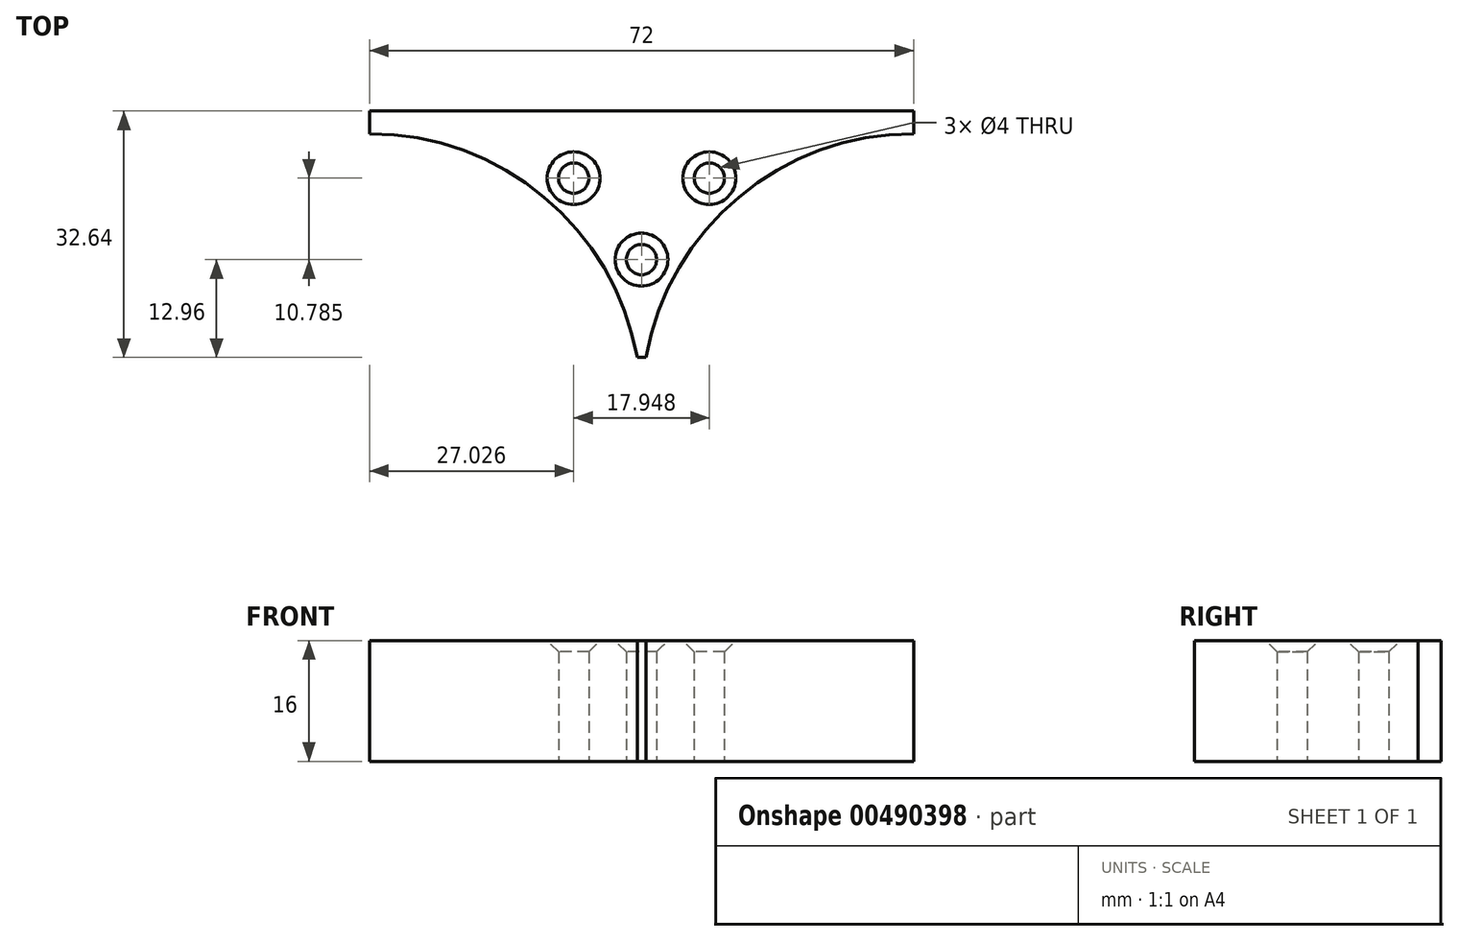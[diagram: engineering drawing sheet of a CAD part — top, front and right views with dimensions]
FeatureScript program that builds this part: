
annotation { "Feature Type Name" : "Feature", "Feature Type Description" : "" }
export const myFeature = defineFeature(function(context is Context, id is Id, definition is map)
    precondition{}
    {
        {
            var Q0;
            Q0=qCreatedBy(makeId("Top.planeOp"),FACE);
            var sketch = newSketch(context, id + "F0", { "sketchPlane" : qUnion([Q0])});
            skArc(sketch, "E0", {"start": v(-0.57, 6.36) * mm, "mid": v(-12.9, 27.61) * mm, "end": v(-36, 36) * mm});
            skArc(sketch, "E1.MirrorC", {"start": v(0.57, 6.36) * mm, "mid": v(12.9, 27.61) * mm, "end": v(36, 36) * mm});
            skLineSegment(sketch, "E2", {"start": v(-0.57, 6.36) * mm, "end": v(0.57, 6.36) * mm});
            skLineSegment(sketch, "E3", {"start": v(-36, 36) * mm, "end": v(-36, 39) * mm});
            skLineSegment(sketch, "E4", {"start": v(-36, 39) * mm, "end": v(0, 39) * mm});
            skLineSegment(sketch, "E5.MirrorCS", {"start": v(-36, 42) * mm, "end": v(-36, 39) * mm});
            skLineSegment(sketch, "E6.MirrorCS", {"start": v(36, 39) * mm, "end": v(0, 39) * mm});
            skLineSegment(sketch, "E7.MirrorCS", {"start": v(36, 36) * mm, "end": v(36, 39) * mm});
            skCircle(sketch, "E8", {"center": v(-36, 0) * mm, "radius": 35.5 * mm, "construction": true});
            skCircle(sketch, "E9", {"center": v(36, 0) * mm, "radius": 35.5 * mm, "construction": true});
            skCircle(sketch, "E10", {"center": v(0, 19.32) * mm, "radius": 2 * mm});
            skCircle(sketch, "E11", {"center": v(-8.97, 30.1) * mm, "radius": 2 * mm});
            skCircle(sketch, "E12.MirrorC", {"center": v(8.97, 30.1) * mm, "radius": 2 * mm});
            skSolve(sketch);
        }
        {
            var Q0;
            Q0=makeQuery(id+"F0.imprint","IMPRINT",FACE,{"disambiguationData":[TD([[makeQuery(id+"F0.imprint","IMPRINT",EDGE,{"derivedFrom":sQuery(id+"F0.wireOp",EDGE,"E0")}),-1.0]])]});
            extrude(context, id + "F1", {"entities" : qUnion([Q0]), "depth" : 16 * mm, "offsetDistance" : 25 * mm});
        }
        {
            var Q0;
            Q0=makeQuery(id+"F1.opExtrude","CAP_EDGE",EDGE,{"disambiguationData":[OSD([sQuery(id+"F0.wireOp",EDGE,"E11")])],"isStart":false});
            var Q1;
            Q1=makeQuery(id+"F1.opExtrude","CAP_EDGE",EDGE,{"disambiguationData":[OSD([sQuery(id+"F0.wireOp",EDGE,"E10")])],"isStart":false});
            var Q2;
            Q2=makeQuery(id+"F1.opExtrude","CAP_EDGE",EDGE,{"disambiguationData":[OSD([sQuery(id+"F0.wireOp",EDGE,"E12.MirrorC")])],"isStart":false});
            chamfer(context, id + "F2", {"entities" : qUnion([Q0, Q1, Q2]), "width" : 1.5 * mm, "tangentPropagation" : true});
        }
    });
